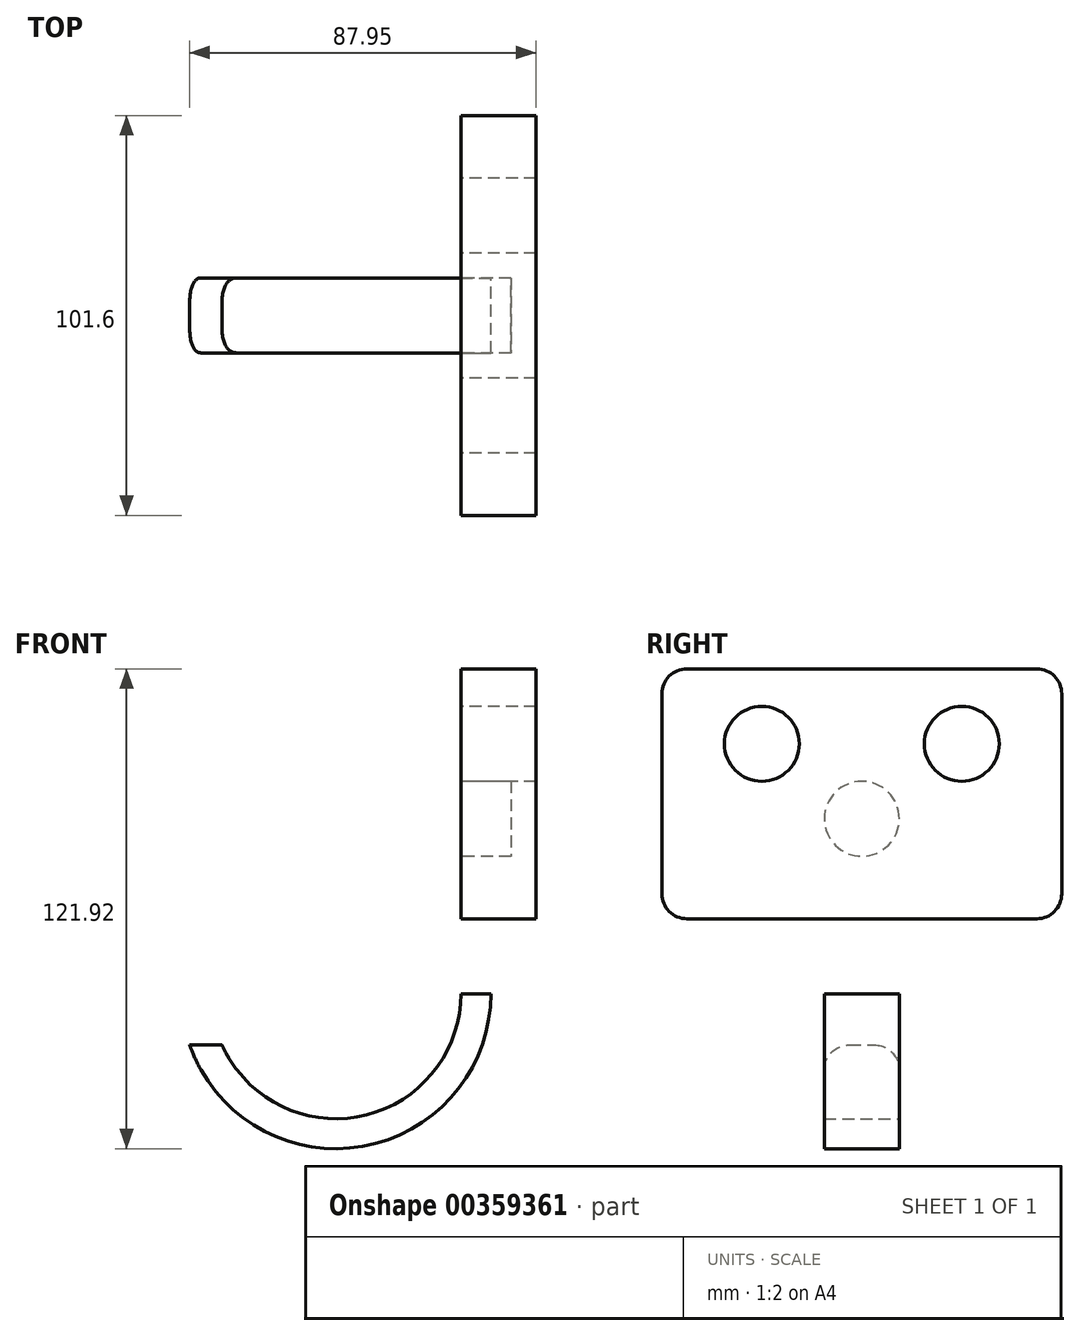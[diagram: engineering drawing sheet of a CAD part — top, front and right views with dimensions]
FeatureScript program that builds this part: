
annotation { "Feature Type Name" : "Feature", "Feature Type Description" : "" }
export const myFeature = defineFeature(function(context is Context, id is Id, definition is map)
    precondition{}
    {
        {
            var Q0;
            Q0=qCreatedBy(makeId("Front.planeOp"),FACE);
            var sketch = newSketch(context, id + "F0", { "sketchPlane" : qUnion([Q0])});
            skLineSegment(sketch, "E0.bottom", {"start": v(0, 0) * mm, "end": v(19.05, 0) * mm});
            skLineSegment(sketch, "E0.top", {"start": v(0, 63.5) * mm, "end": v(19.05, 63.5) * mm});
            skLineSegment(sketch, "E0.left", {"start": v(0, 0) * mm, "end": v(0, 63.5) * mm});
            skLineSegment(sketch, "E0.right", {"start": v(19.05, 0) * mm, "end": v(19.05, 63.5) * mm});
            skLineSegment(sketch, "E1.bottom", {"start": v(0, 0) * mm, "end": v(7.62, 0) * mm});
            skLineSegment(sketch, "E1.top", {"start": v(0, -19.05) * mm, "end": v(7.62, -19.05) * mm});
            skLineSegment(sketch, "E1.left", {"start": v(0, 0) * mm, "end": v(0, -19.05) * mm});
            skLineSegment(sketch, "E1.right", {"start": v(7.62, 0) * mm, "end": v(7.62, -19.05) * mm});
            skArc(sketch, "E2", {"start": v(-71.12, -19.05) * mm, "mid": v(-31.75, -58.42) * mm, "end": v(7.62, -19.05) * mm});
            skArc(sketch, "E3", {"start": v(0, -19.05) * mm, "mid": v(-31.75, -50.8) * mm, "end": v(-63.5, -19.05) * mm});
            skLineSegment(sketch, "E4", {"start": v(-68.9, -32.08) * mm, "end": v(-60.7, -32.08) * mm});
            skSolve(sketch);
        }
        {
            var Q0;
            Q0=makeQuery(id+"F0.imprint","IMPRINT",FACE,{"disambiguationData":[TD([[makeQuery(id+"F0.imprint","IMPRINT",EDGE,{"derivedFrom":sQuery(id+"F0.wireOp",EDGE,"E1.bottom")}),-1.0]])]});
            var Q1;
            {var subQ0=sQuery(id+"F0.wireOp",EDGE,"E1.top");Q1=makeQuery(id+"F0.imprint","IMPRINT",FACE,{"disambiguationData":[TD([[makeQuery(id+"F0.imprint","IMPRINT",EDGE,{"derivedFrom":subQ0}),-1.0]])]});}
            extrude(context, id + "F1", {"entities" : qUnion([Q0, Q1]), "endBound" : BoundingType.SYMMETRIC, "depth" : 19.05 * mm});
        }
        {
            var Q0;
            Q0=makeQuery(id+"F0.imprint","IMPRINT",FACE,{"disambiguationData":[TD([[makeQuery(id+"F0.imprint","IMPRINT",EDGE,{"derivedFrom":sQuery(id+"F0.wireOp",EDGE,"E0.bottom")}),1.0]])]});
            extrude(context, id + "F2", {"entities" : qUnion([Q0]), "endBound" : BoundingType.SYMMETRIC, "depth" : 101.6 * mm});
        }
        {
            var Q0;
            Q0=qCreatedBy(makeId("Right.planeOp"),FACE);
            var sketch = newSketch(context, id + "F3", { "sketchPlane" : qUnion([Q0])});
            skCircle(sketch, "E5", {"center": v(25.4, 44.45) * mm, "radius": 9.53 * mm});
            skCircle(sketch, "E6", {"center": v(-25.4, 44.45) * mm, "radius": 9.53 * mm});
            skSolve(sketch);
        }
        {
            var Q0;
            Q0 = qSketchRegion(id + "F3", true);
            extrude(context, id + "F4", {"entities" : qUnion([Q0]), "operationType" : NewBodyOperationType.REMOVE, "endBound" : BoundingType.THROUGH_ALL, "depth" : 25.4 * mm});
        }
        {
            var Q0;
            Q0=makeQuery(id+"F2.opExtrude","SWEPT_FACE",FACE,{"disambiguationData":[OSD([sQuery(id+"F0.wireOp",EDGE,"E0.left")])]});
            var sketch = newSketch(context, id + "F5", { "sketchPlane" : qUnion([Q0])});
            skCircle(sketch, "E7", {"center": v(0, 25.4) * mm, "radius": 9.53 * mm});
            skSolve(sketch);
        }
        {
            var Q0;
            Q0=makeQuery(id+"F5.imprint","IMPRINT",FACE,{"disambiguationData":[TD([[makeQuery(id+"F5.imprint","IMPRINT",EDGE,{"derivedFrom":sQuery(id+"F5.wireOp",EDGE,"E7")}),1.0]])]});
            extrude(context, id + "F6", {"entities" : qUnion([Q0]), "operationType" : NewBodyOperationType.REMOVE, "oppositeDirection" : true, "depth" : 12.7 * mm});
        }
        {
            var Q0;
            Q0=qCreatedBy(makeId("Right.planeOp"),FACE);
            var sketch = newSketch(context, id + "F7", { "sketchPlane" : qUnion([Q0])});
            skArc(sketch, "E8", {"start": v(50.8, 57.15) * mm, "mid": v(48.94, 61.64) * mm, "end": v(44.45, 63.5) * mm});
            skLineSegment(sketch, "E9", {"start": v(50.8, 57.15) * mm, "end": v(50.8, 63.5) * mm});
            skLineSegment(sketch, "E10", {"start": v(44.45, 63.5) * mm, "end": v(50.8, 63.5) * mm});
            skArc(sketch, "E11", {"start": v(-50.8, 57.15) * mm, "mid": v(-48.94, 61.64) * mm, "end": v(-44.45, 63.5) * mm});
            skLineSegment(sketch, "E12", {"start": v(-44.45, 63.5) * mm, "end": v(-50.8, 63.5) * mm});
            skLineSegment(sketch, "E13", {"start": v(-50.8, 63.5) * mm, "end": v(-50.8, 57.15) * mm});
            skLineSegment(sketch, "E14", {"start": v(-50.8, 57.15) * mm, "end": v(-50.8, 63.5) * mm});
            skArc(sketch, "E15", {"start": v(50.8, 6.35) * mm, "mid": v(48.94, 1.86) * mm, "end": v(44.45, 0) * mm});
            skLineSegment(sketch, "E16", {"start": v(50.8, 6.35) * mm, "end": v(50.8, 0) * mm});
            skLineSegment(sketch, "E17", {"start": v(50.8, 0) * mm, "end": v(44.45, 0) * mm});
            skLineSegment(sketch, "E18", {"start": v(44.45, 0) * mm, "end": v(50.8, 0) * mm});
            skArc(sketch, "E19", {"start": v(-44.45, 0) * mm, "mid": v(-48.94, 1.86) * mm, "end": v(-50.8, 6.35) * mm});
            skLineSegment(sketch, "E20", {"start": v(-44.45, 0) * mm, "end": v(-50.8, 0) * mm});
            skLineSegment(sketch, "E21", {"start": v(-50.8, 0) * mm, "end": v(-50.8, 6.35) * mm});
            skSolve(sketch);
        }
        {
            var Q0;
            Q0 = qSketchRegion(id + "F7", true);
            extrude(context, id + "F8", {"entities" : qUnion([Q0]), "operationType" : NewBodyOperationType.REMOVE, "endBound" : BoundingType.SYMMETRIC, "depth" : 5080 * mm});
        }
        {
            var Q0;
            Q0=makeQuery(id+"F1.opExtrude","CAP_EDGE",EDGE,{"disambiguationData":[OSD([sQuery(id+"F0.wireOp",EDGE,"E4")])],"isStart":true});
            var Q1;
            Q1=makeQuery(id+"F1.opExtrude","CAP_EDGE",EDGE,{"disambiguationData":[OSD([sQuery(id+"F0.wireOp",EDGE,"E4")])],"isStart":false});
            fillet(context, id + "F9", {"entities" : qUnion([Q0, Q1]), "radius" : 6.35 * mm, "tangentPropagation" : true, "allowEdgeOverflow" : false});
        }
    });
